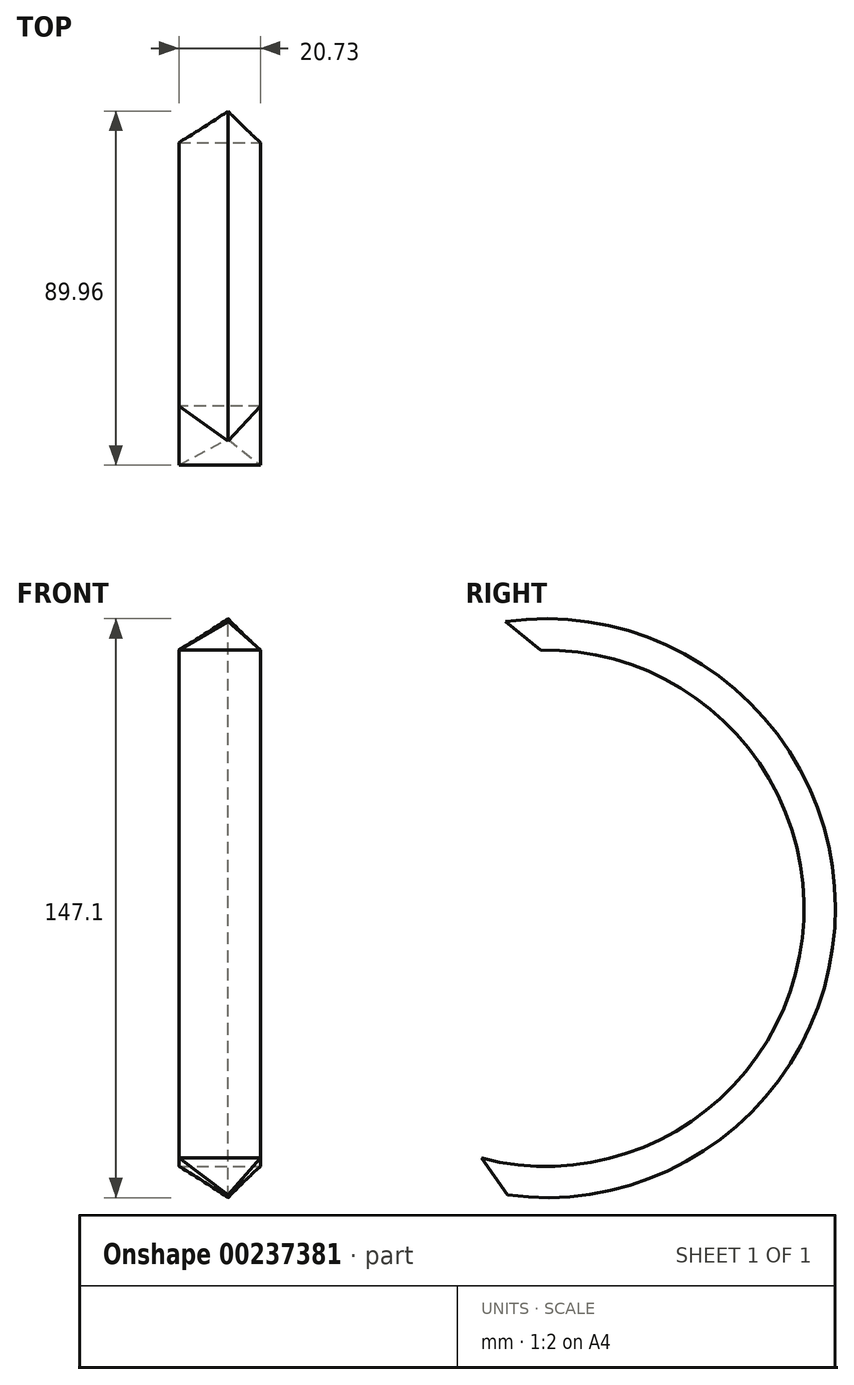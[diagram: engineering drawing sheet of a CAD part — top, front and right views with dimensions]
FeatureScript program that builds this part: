
annotation { "Feature Type Name" : "Feature", "Feature Type Description" : "" }
export const myFeature = defineFeature(function(context is Context, id is Id, definition is map)
    precondition{}
    {
        {
            var Q0;
            Q0=qCreatedBy(makeId("Front.planeOp"),FACE);
            var sketch = newSketch(context, id + "F0", { "sketchPlane" : qUnion([Q0])});
            skLineSegment(sketch, "E0", {"start": v(-28.94, 11.48) * mm, "end": v(-20.72, 0) * mm});
            skLineSegment(sketch, "E1", {"start": v(-20.72, 0) * mm, "end": v(-41.45, 0) * mm});
            skLineSegment(sketch, "E2", {"start": v(-41.45, 0) * mm, "end": v(-28.94, 11.48) * mm});
            skSolve(sketch);
        }
        {
            var Q0;
            Q0=qCreatedBy(makeId("Right.planeOp"),FACE);
            var sketch = newSketch(context, id + "F1", { "sketchPlane" : qUnion([Q0])});
            skArc(sketch, "E3", {"start": v(-52.15, -51.1) * mm, "mid": v(-41.13, -43.55) * mm, "end": v(-50.12, -33.66) * mm});
            skSolve(sketch);
        }
        {
            var Q0;
            Q0=makeQuery(id+"F0.imprint","IMPRINT",FACE,{"disambiguationData":[TD([[makeQuery(id+"F0.imprint","IMPRINT",EDGE,{"derivedFrom":sQuery(id+"F0.wireOp",EDGE,"E0")}),-1.0]])]});
            var Q1;
            Q1=sQuery(id+"F1.wireOp",EDGE,"E3");
            sweep(context, id + "F2", {"profiles" : qUnion([Q0]), "path" : qUnion([Q1])});
        }
    });
